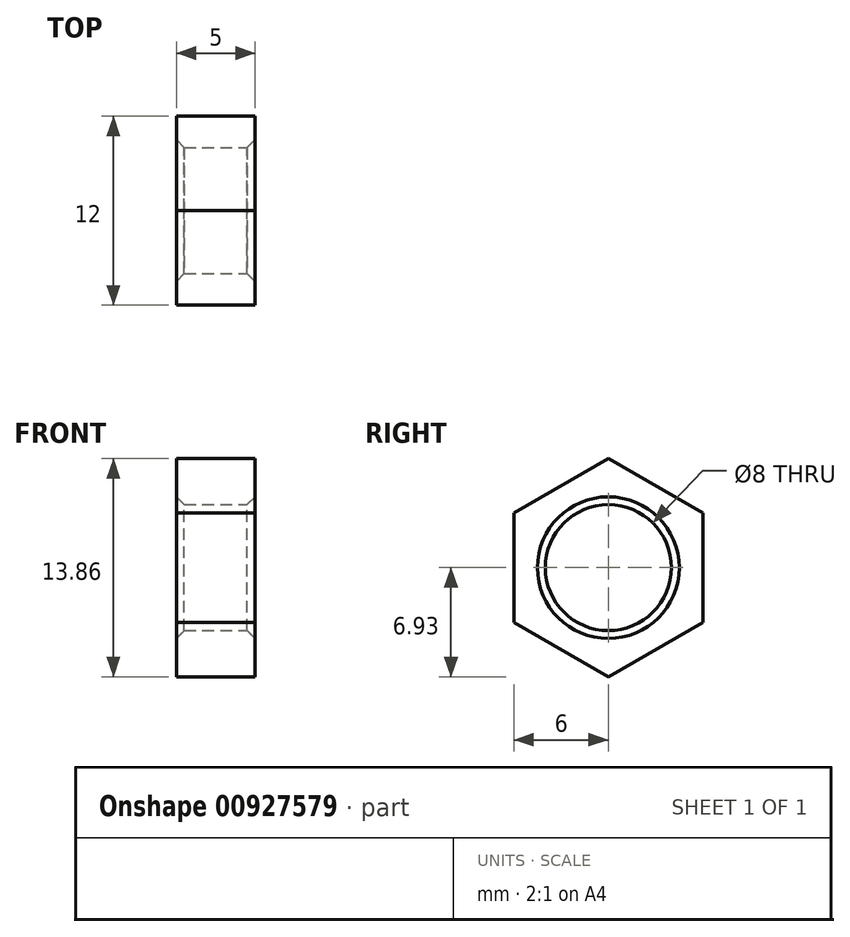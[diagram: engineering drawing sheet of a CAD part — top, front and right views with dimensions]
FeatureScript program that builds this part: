
annotation { "Feature Type Name" : "Feature", "Feature Type Description" : "" }
export const myFeature = defineFeature(function(context is Context, id is Id, definition is map)
    precondition{}
    {
        {
            var Q0;
            Q0=qCreatedBy(makeId("Right.planeOp"),FACE);
            var sketch = newSketch(context, id + "F0", { "sketchPlane" : qUnion([Q0])});
            skLineSegment(sketch, "E0", {"start": v(0, 12.1) * mm, "end": v(0, -15.1) * mm, "construction": true});
            skLineSegment(sketch, "E1", {"start": v(-23.24, 0) * mm, "end": v(20.64, 0) * mm, "construction": true});
            skCircle(sketch, "E2.cCircle", {"center": v(0, 0) * mm, "radius": 6 * mm, "construction": true});
            skLineSegment(sketch, "E2.0", {"start": v(6, -3.46) * mm, "end": v(0, -6.93) * mm});
            skLineSegment(sketch, "E2.1", {"start": v(0, -6.93) * mm, "end": v(-6, -3.46) * mm});
            skLineSegment(sketch, "E2.2", {"start": v(-6, -3.46) * mm, "end": v(-6, 3.46) * mm});
            skLineSegment(sketch, "E2.3", {"start": v(-6, 3.46) * mm, "end": v(0, 6.93) * mm});
            skLineSegment(sketch, "E2.4", {"start": v(0, 6.93) * mm, "end": v(6, 3.46) * mm});
            skLineSegment(sketch, "E2.5", {"start": v(6, 3.46) * mm, "end": v(6, -3.46) * mm});
            skPoint(sketch, "E2.0.midPoint", {"position": v(3, -5.2) * mm});
            skSolve(sketch);
        }
        {
            var Q0;
            Q0 = qSketchRegion(id + "F0", true);
            extrude(context, id + "F1", {"entities" : qUnion([Q0]), "oppositeDirection" : true, "depth" : 5 * mm, "offsetDistance" : 25 * mm});
        }
        {
            var Q0;
            Q0=makeQuery(id+"F1.opExtrude","CAP_FACE",FACE,{"disambiguationData":[OSD([sQuery(id+"F0.wireOp",EDGE,"E2.0"),sQuery(id+"F0.wireOp",EDGE,"E2.1"),sQuery(id+"F0.wireOp",EDGE,"E2.2"),sQuery(id+"F0.wireOp",EDGE,"E2.3"),sQuery(id+"F0.wireOp",EDGE,"E2.4"),sQuery(id+"F0.wireOp",EDGE,"E2.5")])],"isStart":true});
            var sketch = newSketch(context, id + "F2", { "sketchPlane" : qUnion([Q0])});
            skCircle(sketch, "E3", {"center": v(0, 0) * mm, "radius": 4 * mm});
            skSolve(sketch);
        }
        {
            var Q0;
            Q0 = qSketchRegion(id + "F2", true);
            extrude(context, id + "F3", {"entities" : qUnion([Q0]), "operationType" : NewBodyOperationType.REMOVE, "endBound" : BoundingType.THROUGH_ALL, "oppositeDirection" : true, "depth" : 25 * mm, "offsetDistance" : 25 * mm});
        }
        {
            var Q0;
            Q0=makeQuery(id+"F3.boolean.opBoolean","COPY",FACE,{"derivedFrom":makeQuery(id+"F3.opExtrude","SWEPT_FACE",FACE,{"disambiguationData":[OSD([sQuery(id+"F2.wireOp",EDGE,"E3")])]})});
            chamfer(context, id + "F4", {"entities" : qUnion([Q0]), "width" : 0.5 * mm, "tangentPropagation" : true});
        }
    });
